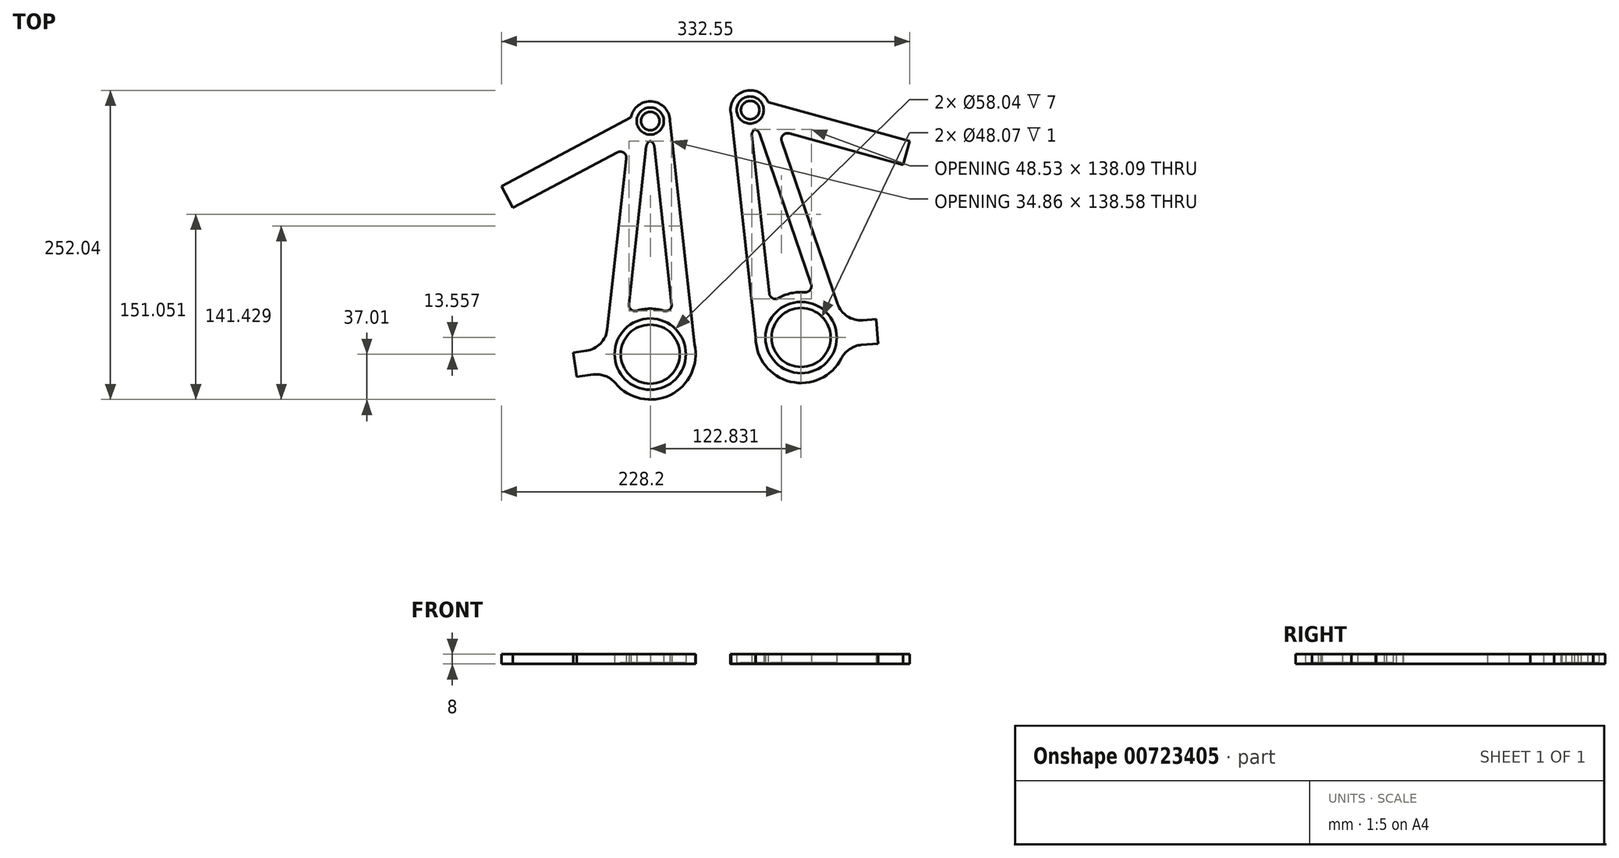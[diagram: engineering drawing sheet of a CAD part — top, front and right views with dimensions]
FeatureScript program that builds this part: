
annotation { "Feature Type Name" : "Feature", "Feature Type Description" : "" }
export const myFeature = defineFeature(function(context is Context, id is Id, definition is map)
    precondition{}
    {
        {
            var Q0;
            Q0=qCreatedBy(makeId("Top.planeOp"),FACE);
            var sketch = newSketch(context, id + "F0", { "sketchPlane" : qUnion([Q0])});
            skPoint(sketch, "E0", {"position": v(0, 0) * mm});
            skPoint(sketch, "E1", {"position": v(0, 190) * mm});
            skCircle(sketch, "E2", {"center": v(0, 190) * mm, "radius": 7.5 * mm});
            skCircle(sketch, "E3", {"center": v(0, 190) * mm, "radius": 11.04 * mm});
            skCircle(sketch, "E4", {"center": v(0, 0) * mm, "radius": 24.03 * mm});
            skCircle(sketch, "E5", {"center": v(0, 0) * mm, "radius": 29.02 * mm});
            skArc(sketch, "E6", {"start": v(-28.46, -23.67) * mm, "mid": v(16.33, -33.22) * mm, "end": v(36.12, 8.07) * mm});
            skLineSegment(sketch, "E7", {"start": v(36.12, 8.07) * mm, "end": v(16.04, 190) * mm});
            skLineSegment(sketch, "E8", {"start": v(-19.43, 159.48) * mm, "end": v(-35.01, 20.37) * mm});
            skLineSegment(sketch, "E9.0", {"start": v(-52.08, 2.8) * mm, "end": v(-62.79, 1.27) * mm});
            skLineSegment(sketch, "E10", {"start": v(-121.24, 136.86) * mm, "end": v(-111.85, 119.2) * mm});
            skLineSegment(sketch, "E11", {"start": v(-62.79, 1.27) * mm, "end": v(-60, -18.53) * mm});
            skLineSegment(sketch, "E12.trimOffspring", {"start": v(-15.77, 192.94) * mm, "end": v(-121.24, 136.86) * mm});
            skLineSegment(sketch, "E13.trimOffspring", {"start": v(-26.74, 164.46) * mm, "end": v(-111.85, 119.2) * mm});
            skArc(sketch, "E14.trimOffspring", {"start": v(16.04, 190) * mm, "mid": v(1.48, 205.97) * mm, "end": v(-15.77, 192.94) * mm});
            skLineSegment(sketch, "E15.trimOffspring", {"start": v(-3.2, 169.58) * mm, "end": v(-17.43, 40.67) * mm});
            skLineSegment(sketch, "E16.trimOffspring", {"start": v(-46.62, -16.65) * mm, "end": v(-60, -18.53) * mm});
            skLineSegment(sketch, "E17.trimOffspring", {"start": v(17.43, 40.67) * mm, "end": v(3.2, 169.58) * mm});
            skArc(sketch, "E18.trimOffspring", {"start": v(10.98, 35.35) * mm, "mid": v(0, 37.01) * mm, "end": v(-10.98, 35.35) * mm});
            skPoint(sketch, "E19.visualSharp", {"position": v(-36.74, 4.97) * mm});
            skPoint(sketch, "E20.visualSharp", {"position": v(-33.9, -14.86) * mm});
            skArc(sketch, "E20.filletArc", {"start": v(-28.46, -23.67) * mm, "mid": v(-36.63, -17.8) * mm, "end": v(-46.62, -16.65) * mm});
            skArc(sketch, "E21.filletArc", {"start": v(-52.08, 2.8) * mm, "mid": v(-40.54, 8.66) * mm, "end": v(-35.01, 20.37) * mm});
            skPoint(sketch, "E22.visualSharp", {"position": v(-18.37, 168.9) * mm});
            skArc(sketch, "E22.filletArc", {"start": v(-19.43, 159.48) * mm, "mid": v(-21.58, 164.18) * mm, "end": v(-26.74, 164.46) * mm});
            skArc(sketch, "E23.filletArc", {"start": v(0, 173.71) * mm, "mid": v(-2.18, 172.1) * mm, "end": v(-3.2, 169.58) * mm});
            skArc(sketch, "E24.filletArc", {"start": v(3.2, 169.58) * mm, "mid": v(2.18, 172.1) * mm, "end": v(0, 173.71) * mm});
            skPoint(sketch, "E25.visualSharp", {"position": v(-18.37, 32.13) * mm});
            skArc(sketch, "E25.filletArc", {"start": v(-17.43, 40.67) * mm, "mid": v(-15.64, 36.26) * mm, "end": v(-10.98, 35.35) * mm});
            skPoint(sketch, "E26.visualSharp", {"position": v(18.37, 32.13) * mm});
            skArc(sketch, "E26.filletArc", {"start": v(10.98, 35.35) * mm, "mid": v(15.64, 36.26) * mm, "end": v(17.43, 40.67) * mm});
            skSolve(sketch);
        }
        {
            var Q0;
            Q0=makeQuery(id+"F0.imprint","IMPRINT",FACE,{"disambiguationData":[TD([[makeQuery(id+"F0.imprint","IMPRINT",EDGE,{"derivedFrom":sQuery(id+"F0.wireOp",EDGE,"E3")}),-1.0]])]});
            extrude(context, id + "F1", {"entities" : qUnion([Q0]), "depth" : 8 * mm, "offsetDistance" : 25 * mm});
        }
        {
            var Q0;
            Q0=makeQuery(id+"F0.imprint","IMPRINT",FACE,{"disambiguationData":[TD([[makeQuery(id+"F0.imprint","IMPRINT",EDGE,{"derivedFrom":sQuery(id+"F0.wireOp",EDGE,"E2")}),-1.0]])]});
            extrude(context, id + "F2", {"entities" : qUnion([Q0]), "operationType" : NewBodyOperationType.ADD, "depth" : 1 * mm, "offsetDistance" : 25 * mm});
        }
        {
            var Q0;
            Q0=makeQuery(id+"F0.imprint","IMPRINT",FACE,{"disambiguationData":[TD([[makeQuery(id+"F0.imprint","IMPRINT",EDGE,{"derivedFrom":sQuery(id+"F0.wireOp",EDGE,"E4")}),-1.0]])]});
            extrude(context, id + "F3", {"entities" : qUnion([Q0]), "operationType" : NewBodyOperationType.ADD, "depth" : 1 * mm, "offsetDistance" : 25 * mm});
        }
        {
            var Q0;
            Q0=makeQuery(id+"F1.opExtrude","SWEPT_FACE",FACE,{"disambiguationData":[OSD([sQuery(id+"F0.wireOp",EDGE,"E7")])]});
            cPlane(context, id + "F4", {"entities" : qUnion([Q0]), "cplaneType" : CPlaneType.OFFSET, "offset" : 25 * mm, "width" : 150 * mm, "height" : 150 * mm});
        }
        {
            var Q0;
            Q0=makeQuery(id+"F1.opExtrude","SWEPT_BODY",BODY,{"disambiguationData":[OSD([sQuery(id+"F0.wireOp",EDGE,"E3"),sQuery(id+"F0.wireOp",EDGE,"E5"),sQuery(id+"F0.wireOp",EDGE,"E6"),sQuery(id+"F0.wireOp",EDGE,"E7"),sQuery(id+"F0.wireOp",EDGE,"E8"),sQuery(id+"F0.wireOp",EDGE,"E9.0"),sQuery(id+"F0.wireOp",EDGE,"E10"),sQuery(id+"F0.wireOp",EDGE,"E11"),sQuery(id+"F0.wireOp",EDGE,"E12.trimOffspring"),sQuery(id+"F0.wireOp",EDGE,"E13.trimOffspring"),sQuery(id+"F0.wireOp",EDGE,"E15.trimOffspring"),sQuery(id+"F0.wireOp",EDGE,"E16.trimOffspring"),sQuery(id+"F0.wireOp",EDGE,"E17.trimOffspring"),sQuery(id+"F0.wireOp",EDGE,"E18.trimOffspring"),sQuery(id+"F0.wireOp",EDGE,"E20.filletArc"),sQuery(id+"F0.wireOp",EDGE,"E21.filletArc"),sQuery(id+"F0.wireOp",EDGE,"E22.filletArc"),sQuery(id+"F0.wireOp",EDGE,"E23.filletArc"),sQuery(id+"F0.wireOp",EDGE,"E24.filletArc"),sQuery(id+"F0.wireOp",EDGE,"E14.trimOffspring"),sQuery(id+"F0.wireOp",EDGE,"E25.filletArc"),sQuery(id+"F0.wireOp",EDGE,"E26.filletArc")])]});
            var Q1;
            Q1=qCreatedBy(id+"F4.planeOp",FACE);
            mirror(context, id + "F5", {"entities" : qUnion([Q0]), "mirrorPlane" : qUnion([Q1])});
        }
    });
